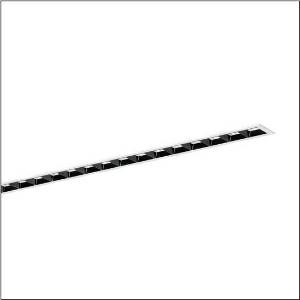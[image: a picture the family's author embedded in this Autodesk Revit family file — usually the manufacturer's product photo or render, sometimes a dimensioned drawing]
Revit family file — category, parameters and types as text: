
# Revit family: silica_r__21_51mx11db35wb_5c76
name_source: partatom
category: Lighting Fixtures
units: mm (PartAtom-declared; Revit-internal decimal feet)

## family parameters
Cut with Voids When Loaded = No
Host = Face
Light Source = No
Part Type = Normal
Room Calculation Point = No
Round Connector Dimension = Use Diameter
Shared = No

## types (1)
- --- (1 x LED, 5400 lm, 34.3 W, 3000K)
    Apparent Load = 34 VA
    CIE Flux Codes = 87 99 100 100 100
    Color Rendering = 80
    Color Temperature = 3000K
    Default Elevation = 1800 mm
    Description = Silica® 21, office luminaire, primary light control with darklight reflector, of PMMA, black, CAT 2 (L<= 3000cd/m²), light emission: direct distribution, primary light characteristic: symmetric, installation type: recessed, LED, rated luminous flux: 5.400lm, luminous efficacy: 157lm/W, light colour: 830, colour temperature: 3000K, control gear: DALI 2, with terminal, 3+2-pole, max. 2.5mm², mains connection: 220..240V, AC, 50/60Hz, rated input power: 34.3W, luminaire housing, of aluminium, traffic white (RAL 9016), length: 1.528mm, width: 79mm, height: 53mm, protection rating (complete): IP20, insulation class (complete): insulation class I (protective earthing), certification: CE, ENEC, VDE, permissible operating ambient temperature: 0..+35°C, standard: EN 50419, packaging unit: 1 piece
    Height = 0 mm  [stored 0 ft]
    Lamp = 1 x LED
    Lamp Light Flux = 5400 lm
    Lamp Power = 34.3 W
    Lamp count = 1
    Length = 1527 mm
    Luminous efficacy = 157 lm/W
    Manufacturer = Siteco
    ModVariant = No
    Model = 51MX11DB35WB
    Mounting Place = Ceiling
    Mounting Type = Recessed
    Number of Poles = 1
    OnlyDefault = Yes
    Power Factor = 1
    Product Name = Silica® 21
    Product group = office luminaire | ceiling recessed
    ProductGroupID = 400
    Protection Class = Protection class I
    Protection Degree = IP 20
    RLX_Detail_Level = 1
    RLX_Emergency_Light_Flux = 0 lm
    RLX_Emergency_Type = 0
    RLX_Emergency_Type_DB = No
    RlxData = <blob elided: 42225 chars, md5=bcb29f74>
    Socket = socket
    Standby Power = 0 W
    System Light Flux = 5400 lm
    System Power = 34 W
    Type Comments = factory setting: luminous flux: 100 % | dim-lin: 254 | 393 mA
    Type Image = l_1335880.jpg
    URL = http://relux.com
    VarID = @adj_144933
    Voltage = 0 V
    Weight = 0.00 kg
    Width = 79 mm

note: [stored X ft] marks values corroborated as IEEE doubles in the binary element streams (Revit-internal decimal feet)

## geometry (parser evidence)
native form markers: Blend x4, Sweep x9
no freeform markers — native parametric forms only
